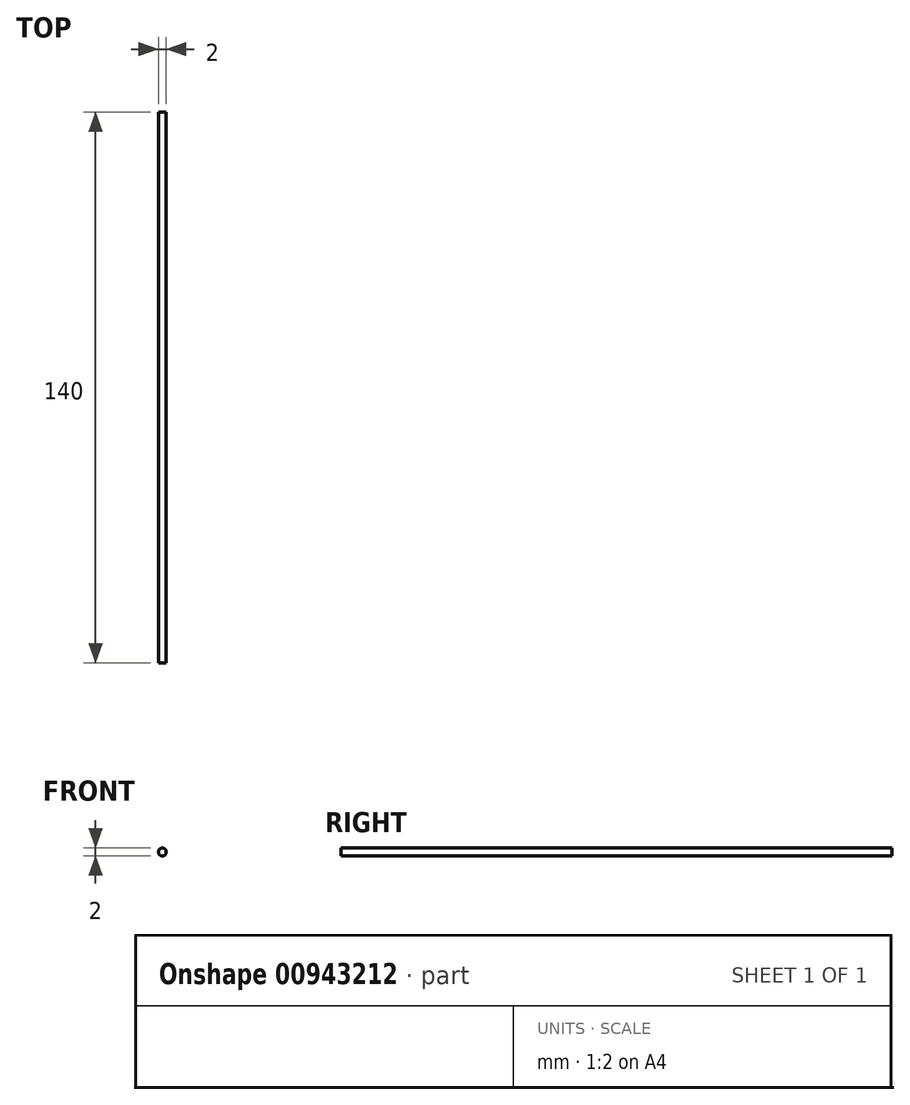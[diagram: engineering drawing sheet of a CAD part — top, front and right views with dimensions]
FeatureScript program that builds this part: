
annotation { "Feature Type Name" : "Feature", "Feature Type Description" : "" }
export const myFeature = defineFeature(function(context is Context, id is Id, definition is map)
    precondition{}
    {
        {
            var Q0;
            Q0=qCreatedBy(makeId("Front.planeOp"),FACE);
            var sketch = newSketch(context, id + "F0", { "sketchPlane" : qUnion([Q0])});
            skCircle(sketch, "E0", {"center": v(0, 0) * mm, "radius": 1 * mm});
            skSolve(sketch);
        }
        {
            var Q0;
            Q0=qSketchRegion(id+"F0",true);
            extrude(context, id + "F1", {"entities" : qUnion([Q0]), "depth" : 140 * mm, "offsetDistance" : 25 * mm});
        }
    });
